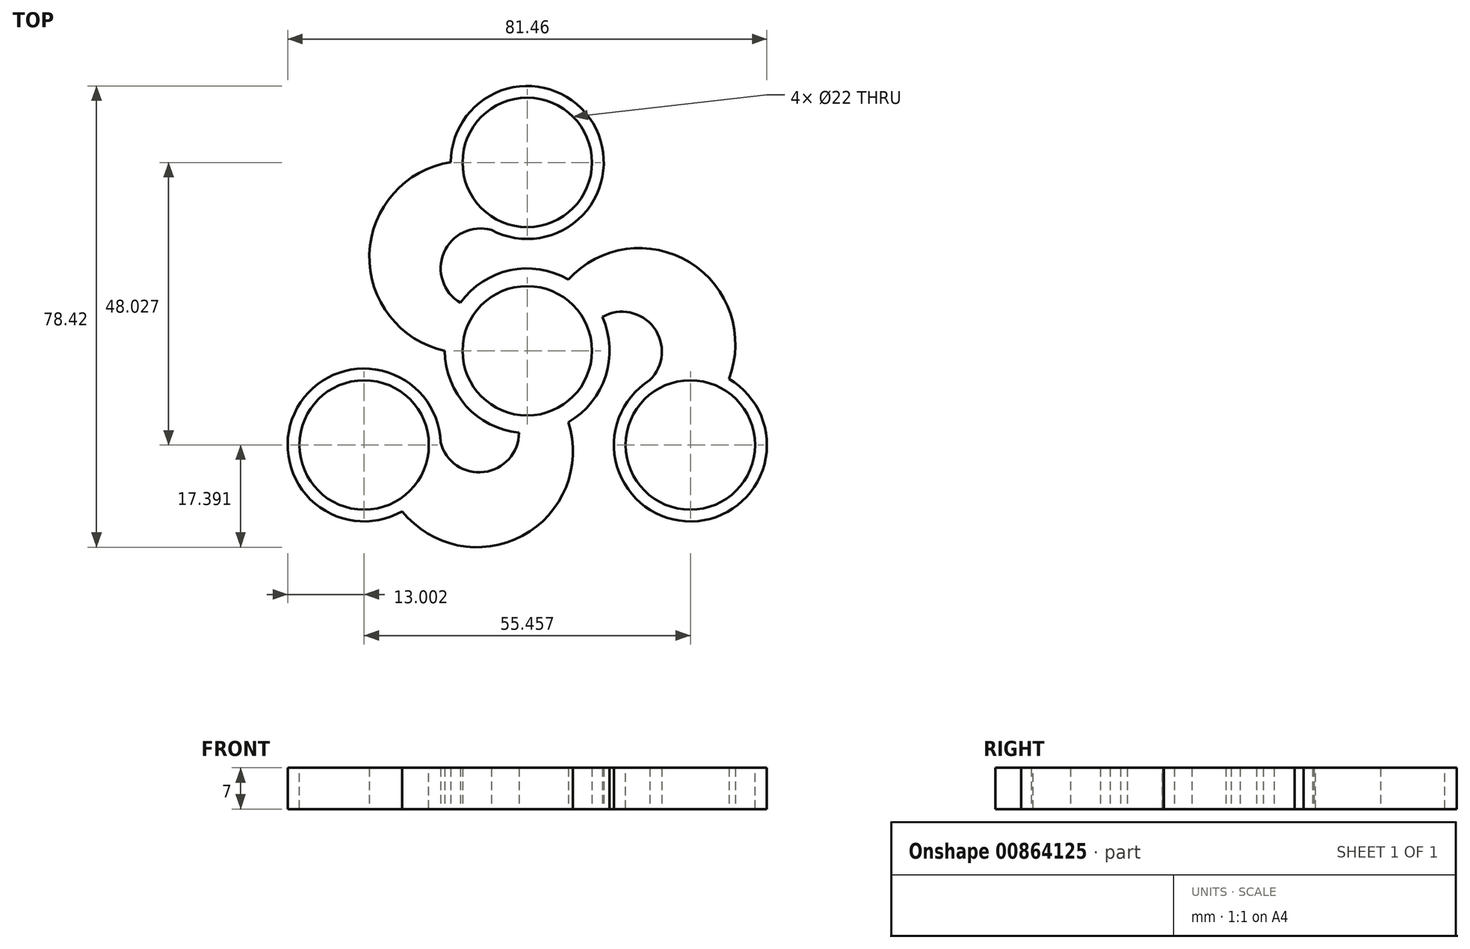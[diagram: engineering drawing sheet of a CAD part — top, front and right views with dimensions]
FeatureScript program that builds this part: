
annotation { "Feature Type Name" : "Feature", "Feature Type Description" : "" }
export const myFeature = defineFeature(function(context is Context, id is Id, definition is map)
    precondition{}
    {
        {
            var Q0;
            Q0=qCreatedBy(makeId("Top.planeOp"),FACE);
            var sketch = newSketch(context, id + "F0", { "sketchPlane" : qUnion([Q0])});
            skCircle(sketch, "E0", {"center": v(0, 0) * mm, "radius": 11 * mm});
            skCircle(sketch, "E1.0", {"center": v(0, 0) * mm, "radius": 14 * mm});
            skCircle(sketch, "E2", {"center": v(0, 0) * mm, "radius": 45 * mm, "construction": true});
            skCircle(sketch, "E3", {"center": v(0, 32.02) * mm, "radius": 13 * mm});
            skArc(sketch, "E4", {"start": v(-13, 32.06) * mm, "mid": v(-26.83, 16.45) * mm, "end": v(-14, 0) * mm});
            skArc(sketch, "E5", {"start": v(-6.1, 20.54) * mm, "mid": v(-14.18, 16.68) * mm, "end": v(-11.36, 8.18) * mm});
            skCircle(sketch, "E6.1.0", {"center": v(-27.73, -16) * mm, "radius": 13 * mm});
            skArc(sketch, "E6.1.1", {"start": v(-21.26, -27.29) * mm, "mid": v(-0.83, -31.46) * mm, "end": v(7, -12.12) * mm});
            skArc(sketch, "E6.1.2", {"start": v(-14.74, -15.55) * mm, "mid": v(-7.36, -20.61) * mm, "end": v(-1.4, -13.93) * mm});
            skCircle(sketch, "E6.2.0", {"center": v(27.73, -16) * mm, "radius": 13 * mm});
            skArc(sketch, "E6.2.1", {"start": v(34.26, -4.77) * mm, "mid": v(27.66, 15.01) * mm, "end": v(7, 12.12) * mm});
            skArc(sketch, "E6.2.2", {"start": v(20.83, -4.99) * mm, "mid": v(21.53, 3.94) * mm, "end": v(12.76, 5.75) * mm});
            skCircle(sketch, "E7", {"center": v(0, 0) * mm, "radius": 45.04 * mm});
            skSolve(sketch);
        }
        {
            var Q0;
            {var subQ0=sQuery(id+"F0.wireOp",EDGE,"E3");var subQ1=makeQuery(id+"F0.imprint","INTERSECT",VERTEX,{"derivedFrom":[subQ0,sQuery(id+"F0.wireOp",EDGE,"E4")]});Q0=makeQuery(id+"F0.imprint","IMPRINT",FACE,{"disambiguationData":[TD([[makeQuery(id+"F0.imprint","IMPRINT",EDGE,{"disambiguationData":[TD([[subQ1,-1.0]])],"derivedFrom":subQ0}),1.0]])]});}
            var Q1;
            {var subQ0=sQuery(id+"F0.wireOp",EDGE,"E4");Q1=makeQuery(id+"F0.imprint","IMPRINT",FACE,{"disambiguationData":[TD([[makeQuery(id+"F0.imprint","IMPRINT",EDGE,{"derivedFrom":subQ0}),1.0]])]});}
            var Q2;
            {var subQ0=sQuery(id+"F0.wireOp",EDGE,"E6.2.1");Q2=makeQuery(id+"F0.imprint","IMPRINT",FACE,{"disambiguationData":[TD([[makeQuery(id+"F0.imprint","IMPRINT",EDGE,{"derivedFrom":subQ0}),1.0]])]});}
            var Q3;
            {var subQ0=sQuery(id+"F0.wireOp",EDGE,"E6.2.0");var subQ1=makeQuery(id+"F0.imprint","INTERSECT",VERTEX,{"derivedFrom":[subQ0,sQuery(id+"F0.wireOp",EDGE,"E6.2.1")]});Q3=makeQuery(id+"F0.imprint","IMPRINT",FACE,{"disambiguationData":[TD([[makeQuery(id+"F0.imprint","IMPRINT",EDGE,{"disambiguationData":[TD([[subQ1,-1.0]])],"derivedFrom":subQ0}),1.0]])]});}
            var Q4;
            {var subQ0=sQuery(id+"F0.wireOp",EDGE,"E6.1.0");var subQ1=makeQuery(id+"F0.imprint","INTERSECT",VERTEX,{"derivedFrom":[subQ0,sQuery(id+"F0.wireOp",EDGE,"E6.1.1")]});Q4=makeQuery(id+"F0.imprint","IMPRINT",FACE,{"disambiguationData":[TD([[makeQuery(id+"F0.imprint","IMPRINT",EDGE,{"disambiguationData":[TD([[subQ1,-1.0]])],"derivedFrom":subQ0}),1.0]])]});}
            var Q5;
            {var subQ0=sQuery(id+"F0.wireOp",EDGE,"E6.1.1");Q5=makeQuery(id+"F0.imprint","IMPRINT",FACE,{"disambiguationData":[TD([[makeQuery(id+"F0.imprint","IMPRINT",EDGE,{"derivedFrom":subQ0}),1.0]])]});}
            var Q6;
            Q6=makeQuery(id+"F0.imprint","IMPRINT",FACE,{"disambiguationData":[TD([[makeQuery(id+"F0.imprint","IMPRINT",EDGE,{"derivedFrom":sQuery(id+"F0.wireOp",EDGE,"E0")}),-1.0]])]});
            extrude(context, id + "F1", {"entities" : qUnion([Q0, Q1, Q2, Q3, Q4, Q5, Q6]), "depth" : 7 * mm, "offsetDistance" : 25 * mm});
        }
        {
            var Q0;
            Q0=makeQuery(id+"F1.opExtrude","CAP_FACE",FACE,{"disambiguationData":[OSD([sQuery(id+"F0.wireOp",EDGE,"E0"),sQuery(id+"F0.wireOp",EDGE,"E1.0"),sQuery(id+"F0.wireOp",EDGE,"E3"),sQuery(id+"F0.wireOp",EDGE,"E4"),sQuery(id+"F0.wireOp",EDGE,"E5"),sQuery(id+"F0.wireOp",EDGE,"E6.1.0"),sQuery(id+"F0.wireOp",EDGE,"E6.1.1"),sQuery(id+"F0.wireOp",EDGE,"E6.1.2"),sQuery(id+"F0.wireOp",EDGE,"E6.2.0"),sQuery(id+"F0.wireOp",EDGE,"E6.2.1"),sQuery(id+"F0.wireOp",EDGE,"E6.2.2")])],"isStart":false});
            var sketch = newSketch(context, id + "F2", { "sketchPlane" : qUnion([Q0])});
            skCircle(sketch, "E8", {"center": v(0, 32.02) * mm, "radius": 11 * mm});
            skCircle(sketch, "E9.1.0", {"center": v(-27.73, -16) * mm, "radius": 11 * mm});
            skCircle(sketch, "E9.2.0", {"center": v(27.73, -16) * mm, "radius": 11 * mm});
            skPoint(sketch, "E9.center", {"position": v(0, 0) * mm});
            skSolve(sketch);
        }
        {
            var Q0;
            Q0=makeQuery(id+"F2.imprint","IMPRINT",FACE,{"disambiguationData":[TD([[makeQuery(id+"F2.imprint","IMPRINT",EDGE,{"derivedFrom":sQuery(id+"F2.wireOp",EDGE,"E8")}),1.0]])]});
            var Q1;
            Q1=makeQuery(id+"F2.imprint","IMPRINT",FACE,{"disambiguationData":[TD([[makeQuery(id+"F2.imprint","IMPRINT",EDGE,{"derivedFrom":sQuery(id+"F2.wireOp",EDGE,"E9.2.0")}),1.0]])]});
            var Q2;
            Q2=makeQuery(id+"F2.imprint","IMPRINT",FACE,{"disambiguationData":[TD([[makeQuery(id+"F2.imprint","IMPRINT",EDGE,{"derivedFrom":sQuery(id+"F2.wireOp",EDGE,"E9.1.0")}),1.0]])]});
            extrude(context, id + "F3", {"entities" : qUnion([Q0, Q1, Q2]), "operationType" : NewBodyOperationType.REMOVE, "oppositeDirection" : true, "depth" : 25 * mm, "offsetDistance" : 25 * mm});
        }
    });
